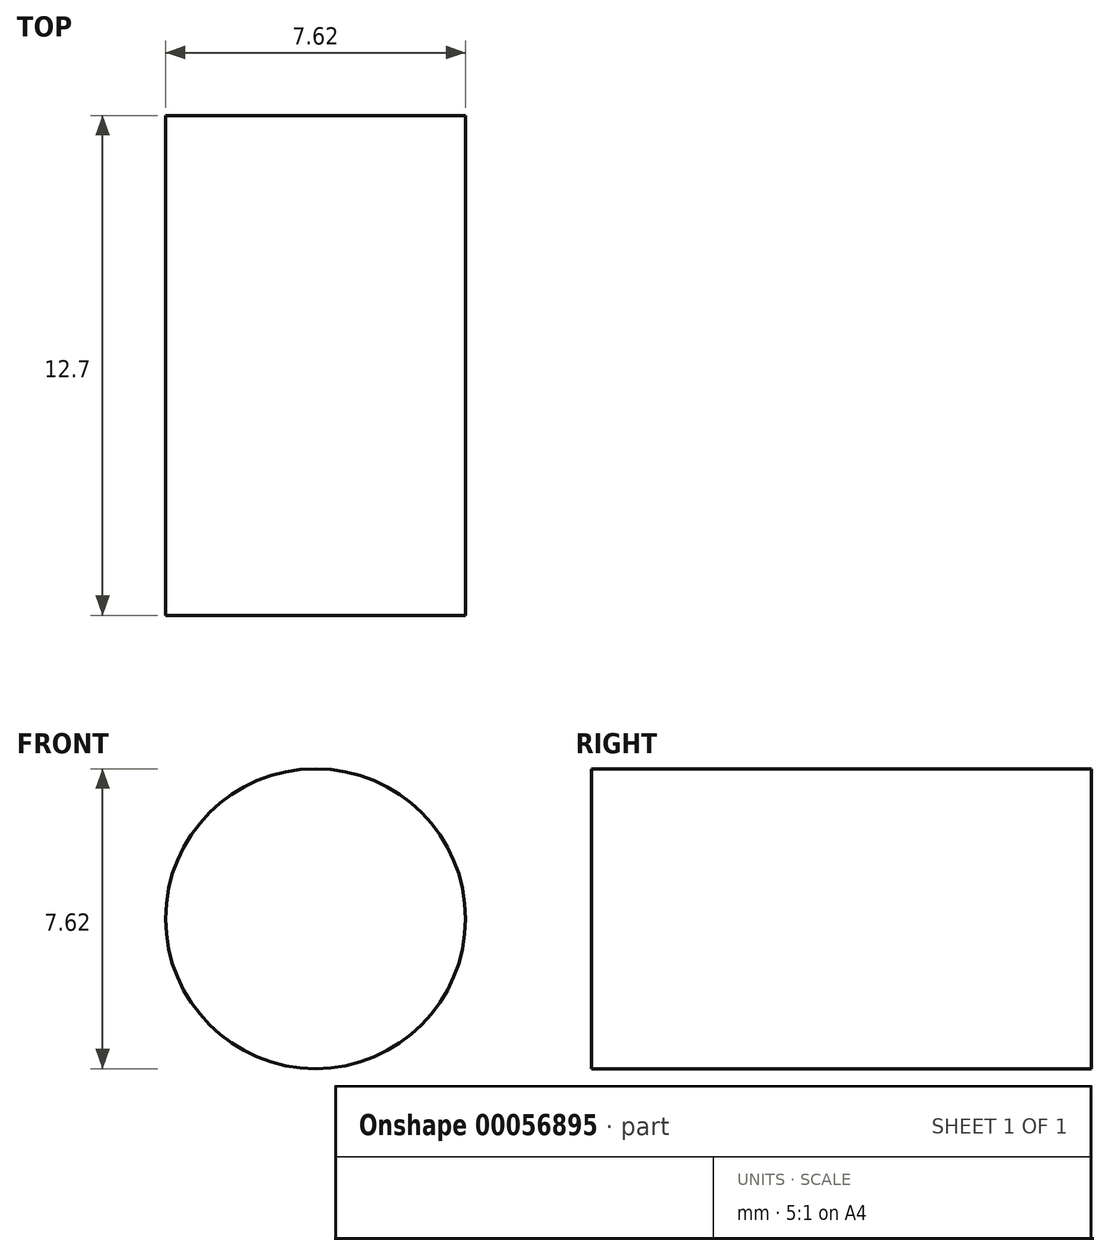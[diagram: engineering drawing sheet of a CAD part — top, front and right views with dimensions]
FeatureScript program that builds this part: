
annotation { "Feature Type Name" : "Feature", "Feature Type Description" : "" }
export const myFeature = defineFeature(function(context is Context, id is Id, definition is map)
    precondition{}
    {
        {
            var Q0;
            Q0=qCreatedBy(makeId("Front.planeOp"),FACE);
            var sketch = newSketch(context, id + "F0", { "sketchPlane" : qUnion([Q0])});
            skCircle(sketch, "E0", {"center": v(0, 0) * mm, "radius": 3.8 * mm});
            skSolve(sketch);
        }
        {
            var Q0;
            Q0=makeQuery(id+"F0.imprint","IMPRINT",FACE,{"disambiguationData":[TD([[makeQuery(id+"F0.imprint","IMPRINT",EDGE,{"derivedFrom":sQuery(id+"F0.wireOp",EDGE,"E0")}),1.0]])]});
            extrude(context, id + "F1", {"entities" : qUnion([Q0]), "endBound" : BoundingType.SYMMETRIC, "depth" : 12.7 * mm});
        }
    });
